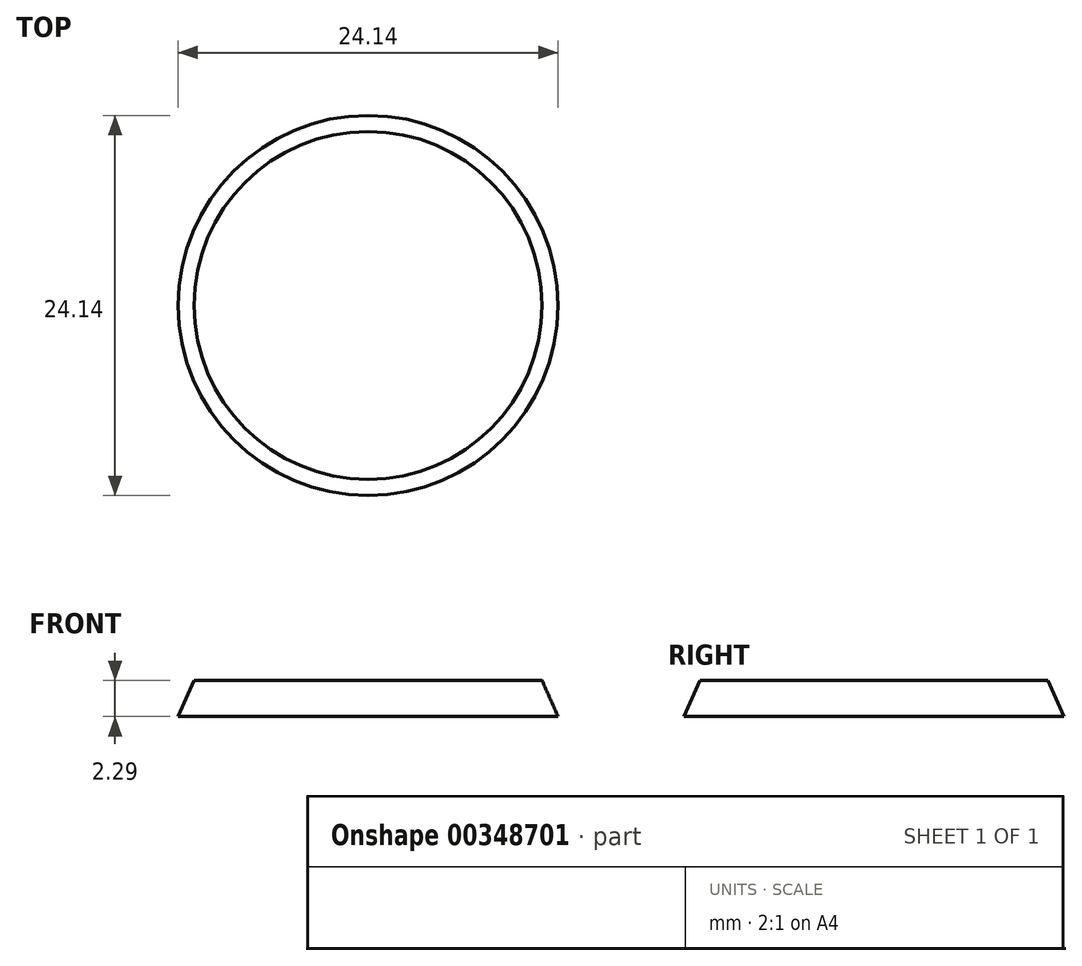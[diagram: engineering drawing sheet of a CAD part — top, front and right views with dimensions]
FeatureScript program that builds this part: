
annotation { "Feature Type Name" : "Feature", "Feature Type Description" : "" }
export const myFeature = defineFeature(function(context is Context, id is Id, definition is map)
    precondition{}
    {
        {
            var Q0;
            Q0=qCreatedBy(makeId("Top.planeOp"),FACE);
            var sketch = newSketch(context, id + "F0", { "sketchPlane" : qUnion([Q0])});
            skLineSegment(sketch, "E0.bottom", {"start": v(31.75, -31.75) * mm, "end": v(-31.75, -31.75) * mm, "construction": true});
            skLineSegment(sketch, "E0.top", {"start": v(31.75, 31.75) * mm, "end": v(-31.75, 31.75) * mm, "construction": true});
            skLineSegment(sketch, "E0.left", {"start": v(31.75, -31.75) * mm, "end": v(31.75, 31.75) * mm, "construction": true});
            skLineSegment(sketch, "E0.right", {"start": v(-31.75, -31.75) * mm, "end": v(-31.75, 31.75) * mm, "construction": true});
            skPoint(sketch, "E0.middle", {"position": v(0, 0) * mm});
            skLineSegment(sketch, "E1", {"start": v(0, 31.75) * mm, "end": v(0, -31.75) * mm, "construction": true});
            skLineSegment(sketch, "E2", {"start": v(-31.75, 0) * mm, "end": v(31.75, 0) * mm, "construction": true});
            skCircle(sketch, "E3", {"center": v(-15.58, 15.86) * mm, "radius": 15.9 * mm, "construction": true});
            skPoint(sketch, "E3.first.point", {"position": v(-15.47, 31.75) * mm});
            skPoint(sketch, "E3.second.point", {"position": v(0, 18.98) * mm});
            skPoint(sketch, "E3.third.point", {"position": v(-14.52, 0) * mm});
            skCircle(sketch, "E4", {"center": v(0, 0) * mm, "radius": 15.88 * mm, "construction": true});
            skSolve(sketch);
        }
        {
            var Q0;
            Q0=qCreatedBy(makeId("Top.planeOp"),FACE);
            var sketch = newSketch(context, id + "F1", { "sketchPlane" : qUnion([Q0])});
            skCircle(sketch, "E5", {"center": v(0, 0) * mm, "radius": 15.88 * mm, "construction": true});
            skCircle(sketch, "E6.0", {"center": v(0, 0) * mm, "radius": 12.06 * mm});
            skLineSegment(sketch, "E7", {"start": v(0, 15.88) * mm, "end": v(0, -15.88) * mm, "construction": true});
            skLineSegment(sketch, "E8", {"start": v(0, 15.88) * mm, "end": v(-1.95, 13.56) * mm, "construction": true});
            skLineSegment(sketch, "E9", {"start": v(-1.95, 13.56) * mm, "end": v(-0.8, 13.56) * mm, "construction": true});
            skLineSegment(sketch, "E10", {"start": v(-0.8, 13.56) * mm, "end": v(-0.8, 12.04) * mm, "construction": true});
            skLineSegment(sketch, "E11.MirrorCS", {"start": v(0, 15.88) * mm, "end": v(1.95, 13.56) * mm, "construction": true});
            skLineSegment(sketch, "E12.MirrorCS", {"start": v(1.95, 13.56) * mm, "end": v(0.8, 13.56) * mm, "construction": true});
            skLineSegment(sketch, "E13.MirrorCS", {"start": v(0.8, 13.56) * mm, "end": v(0.8, 12.04) * mm, "construction": true});
            skSolve(sketch);
        }
        {
            var Q0;
            Q0=qCreatedBy(makeId("Top.planeOp"),FACE);
            cPlane(context, id + "F2", {"entities" : qUnion([Q0]), "cplaneType" : CPlaneType.OFFSET, "offset" : 2.3 * mm, "width" : 152.4 * mm, "height" : 152.4 * mm});
        }
        {
            var Q0;
            Q0=qCreatedBy(id+"F2.planeOp",FACE);
            var sketch = newSketch(context, id + "F3", { "sketchPlane" : qUnion([Q0])});
            skCircle(sketch, "E14.0", {"center": v(0, 0) * mm, "radius": 11.05 * mm});
            skSolve(sketch);
        }
        {
            var Q0;
            Q0=makeQuery(id+"F1.imprint","IMPRINT",FACE,{"disambiguationData":[TD([[makeQuery(id+"F1.imprint","IMPRINT",EDGE,{"derivedFrom":sQuery(id+"F1.wireOp",EDGE,"E6.0")}),1.0]])]});
            var Q1;
            Q1=makeQuery(id+"F3.imprint","IMPRINT",FACE,{"disambiguationData":[TD([[makeQuery(id+"F3.imprint","IMPRINT",EDGE,{"derivedFrom":sQuery(id+"F3.wireOp",EDGE,"E14.0")}),1.0]])]});
            var Q2;
            Q2=sQuery(id+"F1.wireOp",EDGE,"E8");
            var Q3;
            Q3=sQuery(id+"F1.wireOp",EDGE,"E9");
            var Q4;
            Q4=sQuery(id+"F1.wireOp",EDGE,"E10");
            var Q5;
            Q5=sQuery(id+"F1.wireOp",EDGE,"E13.MirrorCS");
            var Q6;
            Q6=sQuery(id+"F1.wireOp",EDGE,"E12.MirrorCS");
            var Q7;
            Q7=sQuery(id+"F1.wireOp",EDGE,"E11.MirrorCS");
            loft(context, id + "F4", {"sheetProfilesArray" : [{ "sheetProfileEntities" : qUnion([Q0]) }, { "sheetProfileEntities" : qUnion([Q1]) }], "wireProfilesArray" : [{ "wireProfileEntities" : qUnion([Q2]) }, { "wireProfileEntities" : qUnion([Q3]) }, { "wireProfileEntities" : qUnion([Q4]) }, { "wireProfileEntities" : qUnion([Q5]) }, { "wireProfileEntities" : qUnion([Q6]) }, { "wireProfileEntities" : qUnion([Q7]) }]});
        }
    });
